# Revit family: TROSTEN BCU
name_source: partatom
category: Mechanical Equipment
units: mm (PartAtom-declared; Revit-internal decimal feet)

## family parameters
Always vertical = Yes
Cut with Voids When Loaded = No
OmniClass Number = 23.75.00.00
OmniClass Title = Climate Control (HVAC)
Part Type = Normal
Room Calculation Point = No
Round Connector Dimension = Use Diameter
Shared = No
Work Plane-Based = No

## types (4) — shared parameters
CD FLOW = 0 GPM
Description = -
FAN ESP = 50
HP = -
HZ = 60
MAX LWT(C) = 12.0
MAX WATER PD = 20
MIN EWT(C) = 6.0
MIN FLOW = 100
Manufacturer = CARRIER
Model = 42TW-12 OR EQUAL
PH = 1
ROWS = 3
SENSIBLE COOLING = 7.10
TOTAL COOLING = 10.93
Type Comments = FCU
Type Mark = FCU
VOLTAGE = 220 V
zero-valued in all types: Default Elevation

## per-type parameters (varying)
| type | D | H | HALF HEIGHT | L | RA PLENUM HEIGHT | RA PLENUM WIDTH | SA DUCT HEIGHT | SA DUCT WIDTH | W |
| TFC H-140 4D CS A5 | 409 mm | 359 mm | 179.5 mm | 680 mm | 255 mm | 1000 mm  [stored 3.28084 ft] | 320 mm | 1165 mm | 1385 mm |
| TFC H-190 4D CS A5 | 460 mm | 410 mm | 205 mm  [stored 0.672572 ft] | 718 mm | 255 mm | 1100 mm | 370 mm | 1200 mm | 1421 mm |
| TFC H-240 4D CS A5 | 511 mm | 461 mm | 230.5 mm | 718 mm | 305 mm  [stored 1.00066 ft] | 1100 mm | 420 mm | 1350 mm | 1575 mm |
| TFC H-190 4D DS A5 | 515 mm | 465 mm  [stored 1.52559 ft] | 232.5 mm  [stored 0.762795 ft] | 730 mm  [stored 2.39501 ft] | 405 mm  [stored 1.32874 ft] | 1340 mm  [stored 4.39633 ft] | 305 mm  [stored 1.00066 ft] | 1100 mm | 1423 mm  [stored 4.66864 ft] |

note: [stored X ft] marks values corroborated as IEEE doubles in the binary element streams (Revit-internal decimal feet)

## geometry (parser evidence)
native form markers: Sweep x3
no freeform markers — native parametric forms only
